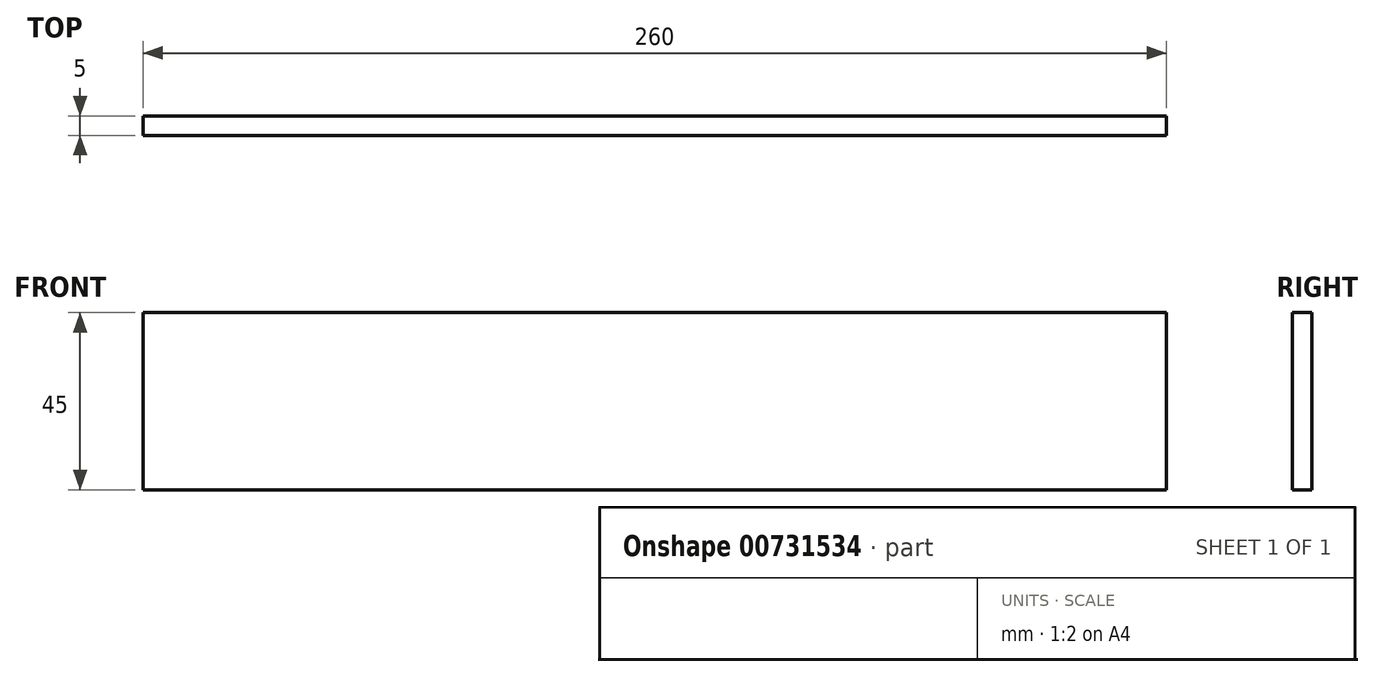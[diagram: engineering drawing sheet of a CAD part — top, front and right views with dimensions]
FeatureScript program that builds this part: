
annotation { "Feature Type Name" : "Feature", "Feature Type Description" : "" }
export const myFeature = defineFeature(function(context is Context, id is Id, definition is map)
    precondition{}
    {
        {
            var Q0;
            Q0=qCreatedBy(makeId("Front.planeOp"),FACE);
            var sketch = newSketch(context, id + "F0", { "sketchPlane" : qUnion([Q0])});
            skLineSegment(sketch, "E0.bottom", {"start": v(0, 0) * mm, "end": v(260, 0) * mm});
            skLineSegment(sketch, "E0.top", {"start": v(0, 45) * mm, "end": v(260, 45) * mm});
            skLineSegment(sketch, "E0.left", {"start": v(0, 0) * mm, "end": v(0, 45) * mm});
            skLineSegment(sketch, "E0.right", {"start": v(260, 0) * mm, "end": v(260, 45) * mm});
            skSolve(sketch);
        }
        {
            var Q0;
            Q0=makeQuery(id+"F0.imprint","IMPRINT",FACE,{"disambiguationData":[TD([[makeQuery(id+"F0.imprint","IMPRINT",EDGE,{"derivedFrom":sQuery(id+"F0.wireOp",EDGE,"E0.bottom")}),1.0]])]});
            extrude(context, id + "F1", {"entities" : qUnion([Q0]), "depth" : 5 * mm, "offsetDistance" : 25 * mm});
        }
    });
